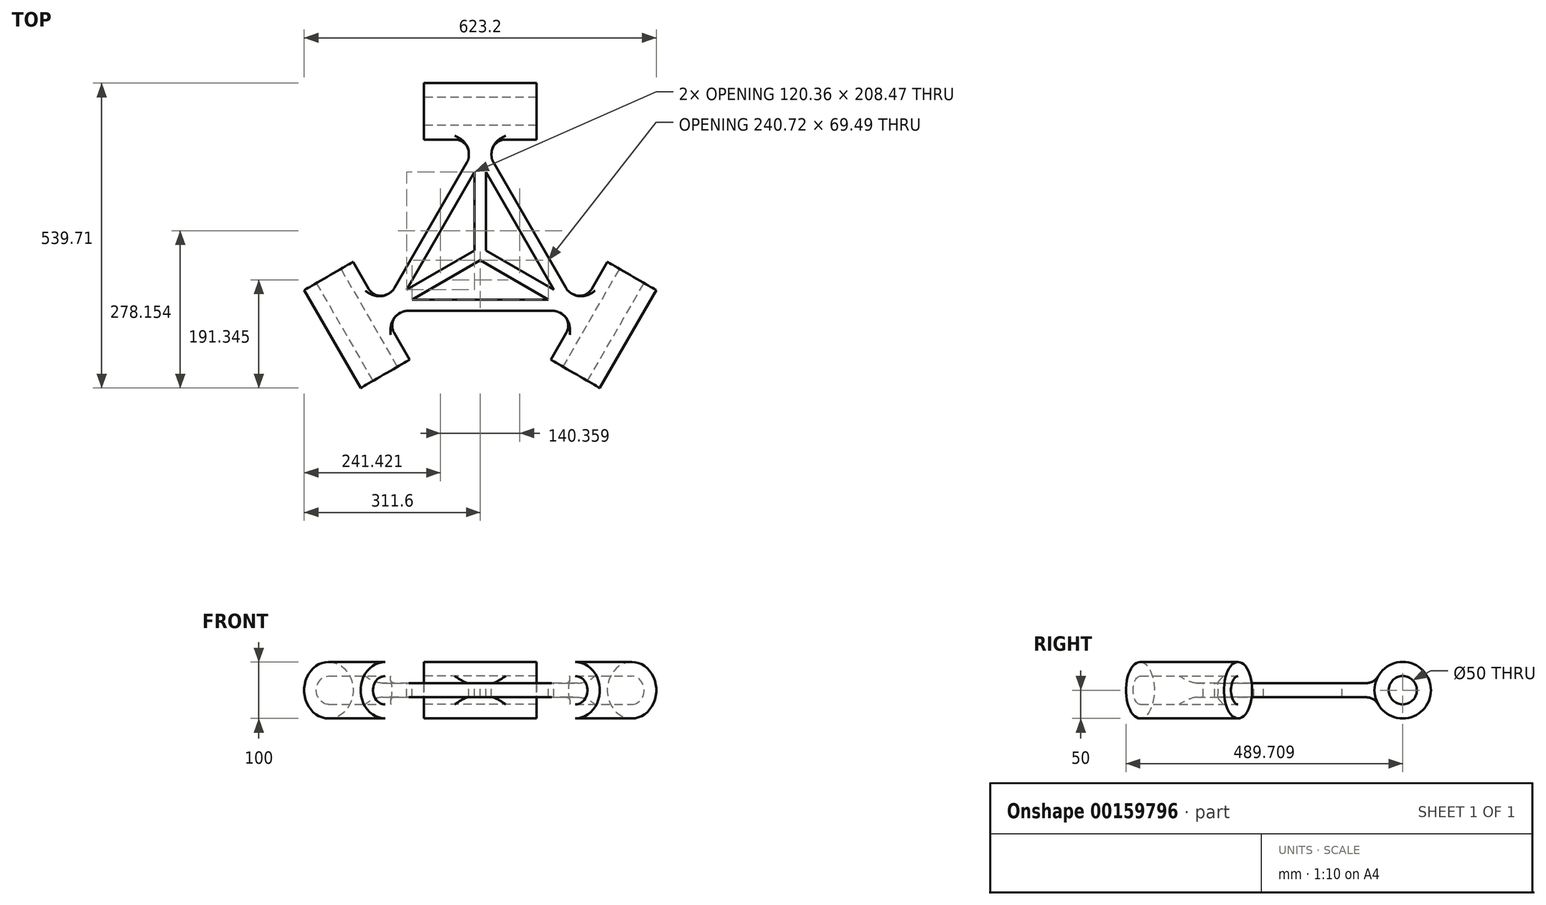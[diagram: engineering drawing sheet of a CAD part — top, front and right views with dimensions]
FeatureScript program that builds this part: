
annotation { "Feature Type Name" : "Feature", "Feature Type Description" : "" }
export const myFeature = defineFeature(function(context is Context, id is Id, definition is map)
    precondition{}
    {
        {
            var Q0;
            Q0=qCreatedBy(makeId("Top.planeOp"),FACE);
            var sketch = newSketch(context, id + "F0", { "sketchPlane" : qUnion([Q0])});
            skLineSegment(sketch, "E0", {"start": v(0, 0) * mm, "end": v(350, 0) * mm});
            skLineSegment(sketch, "E1", {"start": v(0, 0) * mm, "end": v(175, 303.1) * mm});
            skLineSegment(sketch, "E2", {"start": v(175, 303.1) * mm, "end": v(350, 0) * mm});
            skSolve(sketch);
        }
        {
            var Q0;
            Q0=qSketchRegion(id+"F0",true);
            extrude(context, id + "F1", {"entities" : qUnion([Q0]), "depth" : 25 * mm});
        }
        {
            var Q0;
            Q0=qCreatedBy(makeId("Right.planeOp"),FACE);
            var Q1;
            Q1=makeQuery(id+"F1.opExtrude","CAP_VERTEX",VERTEX,{"disambiguationData":[OSD([sQuery(id+"F0.wireOp",EDGE,"E1"),sQuery(id+"F0.wireOp",EDGE,"E2")])],"isStart":false});
            cPlane(context, id + "F2", {"entities" : qUnion([Q0, Q1]), "cplaneType" : CPlaneType.PLANE_POINT, "offset" : 150 * mm, "width" : 150 * mm, "height" : 150 * mm});
        }
        {
            var Q0;
            Q0=qCreatedBy(id+"F2.planeOp",FACE);
            var sketch = newSketch(context, id + "F3", { "sketchPlane" : qUnion([Q0])});
            skLineSegment(sketch, "E3.0", {"start": v(303.1, 25) * mm, "end": v(303.1, 0) * mm});
            skLineSegment(sketch, "E4", {"start": v(303.1, 12.5) * mm, "end": v(353.1, 12.5) * mm});
            skCircle(sketch, "E5", {"center": v(353.1, 12.5) * mm, "radius": 50 * mm});
            skCircle(sketch, "E6", {"center": v(353.1, 12.5) * mm, "radius": 25 * mm});
            skSolve(sketch);
        }
        {
            var Q0;
            Q0=qSketchRegion(id+"F3",true);
            extrude(context, id + "F4", {"entities" : qUnion([Q0]), "endBound" : BoundingType.SYMMETRIC, "depth" : 200 * mm});
        }
        {
            var Q0;
            Q0=makeQuery(id+"F1.opExtrude","CAP_FACE",FACE,{"disambiguationData":[OSD([sQuery(id+"F0.wireOp",EDGE,"E0"),sQuery(id+"F0.wireOp",EDGE,"E1"),sQuery(id+"F0.wireOp",EDGE,"E2")])],"isStart":false});
            var sketch = newSketch(context, id + "F5", { "sketchPlane" : qUnion([Q0])});
            skLineSegment(sketch, "E7", {"start": v(350, 0) * mm, "end": v(87.5, 151.55) * mm});
            skLineSegment(sketch, "E8", {"start": v(0, 0) * mm, "end": v(262.5, 151.55) * mm});
            skSolve(sketch);
        }
        {
            var Q0;
            Q0=qSketchRegion(id+"F5",true);
            var Q1;
            {var subQ1=makeQuery(id+"F1.opExtrude","CAP_EDGE",EDGE,{"disambiguationData":[OSD([sQuery(id+"F0.wireOp",EDGE,"E2")])],"isStart":false});var subQ3=sQuery(id+"F5.wireOp",EDGE,"E8");var subQ5=makeQuery(id+"F5.imprint","INTERSECT",VERTEX,{"derivedFrom":[subQ1,subQ3]});Q1=makeQuery(id+"F5.imprint","IMPRINT",FACE,{"disambiguationData":[TD([[makeQuery(id+"F5.imprint","IMPRINT",EDGE,{"disambiguationData":[TD([[subQ5,1.0]])],"derivedFrom":subQ3}),-1.0]])]});}
            var Q2;
            {var subQ0=sQuery(id+"F5.wireOp",EDGE,"E7");var subQ1=makeQuery(id+"F1.opExtrude","CAP_EDGE",EDGE,{"disambiguationData":[OSD([sQuery(id+"F0.wireOp",EDGE,"E1")])],"isStart":false});var subQ2=makeQuery(id+"F5.imprint","INTERSECT",VERTEX,{"derivedFrom":[subQ1,subQ0]});Q2=makeQuery(id+"F5.imprint","IMPRINT",FACE,{"disambiguationData":[TD([[makeQuery(id+"F5.imprint","IMPRINT",EDGE,{"disambiguationData":[TD([[subQ2,1.0]])],"derivedFrom":subQ0}),1.0]])]});}
            var Q3;
            {var subQ1=makeQuery(id+"F1.opExtrude","CAP_EDGE",EDGE,{"disambiguationData":[OSD([sQuery(id+"F0.wireOp",EDGE,"E0")])],"isStart":false});Q3=makeQuery(id+"F5.imprint","IMPRINT",FACE,{"disambiguationData":[TD([[makeQuery(id+"F5.imprint","IMPRINT",EDGE,{"derivedFrom":subQ1}),1.0]])]});}
            extrude(context, id + "F6", {"entities" : qUnion([Q0, Q1, Q2, Q3]), "operationType" : NewBodyOperationType.REMOVE, "endBound" : BoundingType.THROUGH_ALL, "oppositeDirection" : true, "depth" : 25 * mm});
        }
        {
            var Q0;
            Q0=qCreatedBy(makeId("Front.planeOp"),FACE);
            var Q1;
            Q1=makeQuery(id+"F1.opExtrude","CAP_VERTEX",VERTEX,{"disambiguationData":[OSD([sQuery(id+"F0.wireOp",EDGE,"E1"),sQuery(id+"F0.wireOp",EDGE,"E2")])],"isStart":false});
            cPlane(context, id + "F7", {"entities" : qUnion([Q0, Q1]), "cplaneType" : CPlaneType.PLANE_POINT, "offset" : 150 * mm, "width" : 150 * mm, "height" : 150 * mm});
        }
        {
            var Q0;
            Q0=qCreatedBy(id+"F7.planeOp",FACE);
            var sketch = newSketch(context, id + "F8", { "sketchPlane" : qUnion([Q0])});
            skLineSegment(sketch, "E9.0", {"start": v(175, 0) * mm, "end": v(175, 25) * mm});
            skLineSegment(sketch, "E10", {"start": v(175, 25) * mm, "end": v(155, 25) * mm});
            skLineSegment(sketch, "E11.bottom", {"start": v(155, 25) * mm, "end": v(195, 25) * mm});
            skLineSegment(sketch, "E11.top", {"start": v(155, 0) * mm, "end": v(195, 0) * mm});
            skLineSegment(sketch, "E11.left", {"start": v(155, 25) * mm, "end": v(155, 0) * mm});
            skLineSegment(sketch, "E11.right", {"start": v(195, 25) * mm, "end": v(195, 0) * mm});
            skSolve(sketch);
        }
        {
            var Q0;
            Q0=qSketchRegion(id+"F8",true);
            var Q1;
            Q1=makeQuery(id+"F1.opExtrude","SWEPT_BODY",BODY,{"disambiguationData":[OSD([sQuery(id+"F0.wireOp",EDGE,"E0"),sQuery(id+"F0.wireOp",EDGE,"E1"),sQuery(id+"F0.wireOp",EDGE,"E2")])]});
            extrude(context, id + "F9", {"entities" : qUnion([Q0]), "endBoundEntityBody" : qUnion([Q1]), "depth" : 50 * mm});
        }
        {
            var Q0;
            Q0=makeQuery(id+"F9.opExtrude","SWEPT_BODY",BODY,{"disambiguationData":[OSD([sQuery(id+"F8.wireOp",EDGE,"E11.bottom"),sQuery(id+"F8.wireOp",EDGE,"E11.top"),sQuery(id+"F8.wireOp",EDGE,"E11.left"),sQuery(id+"F8.wireOp",EDGE,"E11.right")])]});
            var Q1;
            Q1=makeQuery(id+"F1.opExtrude","SWEPT_BODY",BODY,{"disambiguationData":[OSD([sQuery(id+"F0.wireOp",EDGE,"E0"),sQuery(id+"F0.wireOp",EDGE,"E1"),sQuery(id+"F0.wireOp",EDGE,"E2")])]});
            booleanBodies(context, id + "F10", {"operationType" : BooleanOperationType.UNION, "tools" : qUnion([Q0, Q1])});
        }
        {
            var Q0;
            Q0=makeQuery(id+"F9.opExtrude","CAP_FACE",FACE,{"disambiguationData":[OSD([sQuery(id+"F8.wireOp",EDGE,"E11.bottom"),sQuery(id+"F8.wireOp",EDGE,"E11.top"),sQuery(id+"F8.wireOp",EDGE,"E11.left"),sQuery(id+"F8.wireOp",EDGE,"E11.right")])],"isStart":true});
            extrude(context, id + "F11", {"entities" : qUnion([Q0]), "depth" : 15 * mm});
        }
        {
            var Q0;
            Q0=makeQuery(id+"F11.opExtrude","SWEPT_BODY",BODY,{"disambiguationData":[OSD([sQuery(id+"F8.wireOp",EDGE,"E11.bottom"),sQuery(id+"F8.wireOp",EDGE,"E11.top"),sQuery(id+"F8.wireOp",EDGE,"E11.left"),sQuery(id+"F8.wireOp",EDGE,"E11.right")])]});
            var Q1;
            Q1=makeQuery(id+"F9.opExtrude","SWEPT_BODY",BODY,{"disambiguationData":[OSD([sQuery(id+"F8.wireOp",EDGE,"E11.bottom"),sQuery(id+"F8.wireOp",EDGE,"E11.top"),sQuery(id+"F8.wireOp",EDGE,"E11.left"),sQuery(id+"F8.wireOp",EDGE,"E11.right")])]});
            booleanBodies(context, id + "F12", {"operationType" : BooleanOperationType.UNION, "tools" : qUnion([Q0, Q1])});
        }
        {
            var Q0;
            Q0=makeQuery(id+"F4.opExtrude","SWEPT_BODY",BODY,{"disambiguationData":[OSD([sQuery(id+"F3.wireOp",EDGE,"E5"),sQuery(id+"F3.wireOp",EDGE,"E6")])]});
            var Q1;
            Q1=makeQuery(id+"F11.opExtrude","SWEPT_BODY",BODY,{"disambiguationData":[OSD([sQuery(id+"F8.wireOp",EDGE,"E11.bottom"),sQuery(id+"F8.wireOp",EDGE,"E11.top"),sQuery(id+"F8.wireOp",EDGE,"E11.left"),sQuery(id+"F8.wireOp",EDGE,"E11.right")])]});
            booleanBodies(context, id + "F13", {"operationType" : BooleanOperationType.UNION, "tools" : qUnion([Q0, Q1])});
        }
        {
            var Q0;
            {var subQ0=sQuery(id+"F8.wireOp",EDGE,"E11.bottom");Q0=makeQuery(id+"F13.opBoolean","INTERSECT",EDGE,{"derivedFrom":[makeQuery(id+"F4.opExtrude","SWEPT_FACE",FACE,{"disambiguationData":[OSD([sQuery(id+"F3.wireOp",EDGE,"E5")])]}),makeQuery(id+"F12.opBoolean","MERGE",FACE,{"derivedFrom":[makeQuery(id+"F10.opBoolean","MERGE",FACE,{"derivedFrom":[makeQuery(id+"F1.opExtrude","CAP_FACE",FACE,{"disambiguationData":[OSD([sQuery(id+"F0.wireOp",EDGE,"E0"),sQuery(id+"F0.wireOp",EDGE,"E1"),sQuery(id+"F0.wireOp",EDGE,"E2")])],"isStart":false}),makeQuery(id+"F9.opExtrude","SWEPT_FACE",FACE,{"disambiguationData":[OSD([subQ0])]})]}),makeQuery(id+"F11.opExtrude","SWEPT_FACE",FACE,{"disambiguationData":[OSD([subQ0])]})]})]});}
            var Q1;
            {var subQ0=sQuery(id+"F8.wireOp",EDGE,"E11.top");Q1=makeQuery(id+"F13.opBoolean","INTERSECT",EDGE,{"derivedFrom":[makeQuery(id+"F4.opExtrude","SWEPT_FACE",FACE,{"disambiguationData":[OSD([sQuery(id+"F3.wireOp",EDGE,"E5")])]}),makeQuery(id+"F12.opBoolean","MERGE",FACE,{"derivedFrom":[makeQuery(id+"F10.opBoolean","MERGE",FACE,{"derivedFrom":[makeQuery(id+"F1.opExtrude","CAP_FACE",FACE,{"disambiguationData":[OSD([sQuery(id+"F0.wireOp",EDGE,"E0"),sQuery(id+"F0.wireOp",EDGE,"E1"),sQuery(id+"F0.wireOp",EDGE,"E2")])],"isStart":true}),makeQuery(id+"F9.opExtrude","SWEPT_FACE",FACE,{"disambiguationData":[OSD([subQ0])]})]}),makeQuery(id+"F11.opExtrude","SWEPT_FACE",FACE,{"disambiguationData":[OSD([subQ0])]})]})]});}
            fillet(context, id + "F14", {"entities" : qUnion([Q0, Q1]), "radius" : 25 * mm, "tangentPropagation" : true, "allowEdgeOverflow" : false});
        }
        {
            var Q0;
            {var subQ0=sQuery(id+"F8.wireOp",EDGE,"E11.right");Q0=makeQuery(id+"F13.opBoolean","INTERSECT",EDGE,{"derivedFrom":[makeQuery(id+"F4.opExtrude","SWEPT_FACE",FACE,{"disambiguationData":[OSD([sQuery(id+"F3.wireOp",EDGE,"E5")])]}),makeQuery(id+"F12.opBoolean","MERGE",FACE,{"derivedFrom":[makeQuery(id+"F9.opExtrude","SWEPT_FACE",FACE,{"disambiguationData":[OSD([subQ0])]}),makeQuery(id+"F11.opExtrude","SWEPT_FACE",FACE,{"disambiguationData":[OSD([subQ0])]})]})]});}
            var Q1;
            {var subQ0=sQuery(id+"F8.wireOp",EDGE,"E11.left");Q1=makeQuery(id+"F13.opBoolean","INTERSECT",EDGE,{"derivedFrom":[makeQuery(id+"F4.opExtrude","SWEPT_FACE",FACE,{"disambiguationData":[OSD([sQuery(id+"F3.wireOp",EDGE,"E5")])]}),makeQuery(id+"F12.opBoolean","MERGE",FACE,{"derivedFrom":[makeQuery(id+"F9.opExtrude","SWEPT_FACE",FACE,{"disambiguationData":[OSD([subQ0])]}),makeQuery(id+"F11.opExtrude","SWEPT_FACE",FACE,{"disambiguationData":[OSD([subQ0])]})]})]});}
            fillet(context, id + "F15", {"entities" : qUnion([Q0, Q1]), "radius" : 25 * mm, "tangentPropagation" : true, "allowEdgeOverflow" : false});
        }
        {
            var Q0;
            Q0=makeQuery(id+"F10.opBoolean","INTERSECT",EDGE,{"derivedFrom":[makeQuery(id+"F1.opExtrude","SWEPT_FACE",FACE,{"disambiguationData":[OSD([sQuery(id+"F0.wireOp",EDGE,"E1")])]}),makeQuery(id+"F9.opExtrude","SWEPT_FACE",FACE,{"disambiguationData":[OSD([sQuery(id+"F8.wireOp",EDGE,"E11.left")])]})]});
            var Q1;
            Q1=makeQuery(id+"F10.opBoolean","INTERSECT",EDGE,{"derivedFrom":[makeQuery(id+"F1.opExtrude","SWEPT_FACE",FACE,{"disambiguationData":[OSD([sQuery(id+"F0.wireOp",EDGE,"E2")])]}),makeQuery(id+"F9.opExtrude","SWEPT_FACE",FACE,{"disambiguationData":[OSD([sQuery(id+"F8.wireOp",EDGE,"E11.right")])]})]});
            fillet(context, id + "F16", {"entities" : qUnion([Q0, Q1]), "radius" : 25 * mm, "tangentPropagation" : true, "allowEdgeOverflow" : false});
        }
        {
            var Q0;
            Q0=qCreatedBy(makeId("Right.planeOp"),FACE);
            var Q1;
            Q1=makeQuery(id+"F6.boolean.opBoolean","COPY",VERTEX,{"derivedFrom":makeQuery(id+"F6.opExtrude","CAP_VERTEX",VERTEX,{"disambiguationData":[OSD([sQuery(id+"F5.wireOp",EDGE,"E7"),sQuery(id+"F5.wireOp",EDGE,"E8")])],"isStart":true})});
            cPlane(context, id + "F17", {"entities" : qUnion([Q0, Q1]), "cplaneType" : CPlaneType.PLANE_POINT, "offset" : 150 * mm, "width" : 150 * mm, "height" : 150 * mm});
        }
        {
            var Q0;
            Q0=qCreatedBy(id+"F17.planeOp",FACE);
            var sketch = newSketch(context, id + "F18", { "sketchPlane" : qUnion([Q0])});
            skLineSegment(sketch, "E12.0", {"start": v(101.04, 0) * mm, "end": v(101.04, 25) * mm});
            skLineSegment(sketch, "E13", {"start": v(101.04, 25) * mm, "end": v(101.04, 40.8) * mm});
            skSolve(sketch);
        }
        {
            var Q0;
            Q0=makeQuery(id+"F4.opExtrude","SWEPT_BODY",BODY,{"disambiguationData":[OSD([sQuery(id+"F3.wireOp",EDGE,"E5"),sQuery(id+"F3.wireOp",EDGE,"E6")])]});
            var Q1;
            Q1=sQuery(id+"F18.wireOp",EDGE,"E13");
            circularPattern(context, id + "F19", {"entities" : qUnion([Q0]), "axis" : qUnion([Q1]), "angle" : 120 * degree, "instanceCount" : 3});
        }
        {
            var Q0;
            Q0=makeQuery(id+"F4.opExtrude","SWEPT_BODY",BODY,{"disambiguationData":[OSD([sQuery(id+"F3.wireOp",EDGE,"E5"),sQuery(id+"F3.wireOp",EDGE,"E6")])]});
            var Q1;
            Q1=makeQuery(id+"F19.opPattern","COPY",BODY,{"derivedFrom":makeQuery(id+"F4.opExtrude","SWEPT_BODY",BODY,{"disambiguationData":[OSD([sQuery(id+"F3.wireOp",EDGE,"E5"),sQuery(id+"F3.wireOp",EDGE,"E6")])]}),"instanceName":"2"});
            var Q2;
            Q2=makeQuery(id+"F19.opPattern","COPY",BODY,{"derivedFrom":makeQuery(id+"F4.opExtrude","SWEPT_BODY",BODY,{"disambiguationData":[OSD([sQuery(id+"F3.wireOp",EDGE,"E5"),sQuery(id+"F3.wireOp",EDGE,"E6")])]}),"instanceName":"1"});
            booleanBodies(context, id + "F20", {"operationType" : BooleanOperationType.UNION, "tools" : qUnion([Q0, Q1, Q2])});
        }
        {
            var Q0;
            {var subQ0=sQuery(id+"F8.wireOp",EDGE,"E11.bottom");var subQ1=makeQuery(id+"F12.opBoolean","MERGE",FACE,{"derivedFrom":[makeQuery(id+"F10.opBoolean","MERGE",FACE,{"derivedFrom":[makeQuery(id+"F1.opExtrude","CAP_FACE",FACE,{"disambiguationData":[OSD([sQuery(id+"F0.wireOp",EDGE,"E0"),sQuery(id+"F0.wireOp",EDGE,"E1"),sQuery(id+"F0.wireOp",EDGE,"E2")])],"isStart":false}),makeQuery(id+"F9.opExtrude","SWEPT_FACE",FACE,{"disambiguationData":[OSD([subQ0])]})]}),makeQuery(id+"F11.opExtrude","SWEPT_FACE",FACE,{"disambiguationData":[OSD([subQ0])]})]});Q0=makeQuery(id+"F20.opBoolean","MERGE",FACE,{"derivedFrom":[subQ1,makeQuery(id+"F19.opPattern","COPY",FACE,{"derivedFrom":subQ1,"instanceName":"1"}),makeQuery(id+"F19.opPattern","COPY",FACE,{"derivedFrom":subQ1,"instanceName":"2"})]});}
            var sketch = newSketch(context, id + "F21", { "sketchPlane" : qUnion([Q0])});
            skLineSegment(sketch, "E14.0.0", {"start": v(151.65, 262.67) * mm, "end": v(23.35, 40.44) * mm});
            skArc(sketch, "E14.0.1", {"start": v(23.35, 40.44) * mm, "mid": v(19.38, 35.26) * mm, "end": v(14.2, 31.3) * mm});
            skLineSegment(sketch, "E14.0.2", {"start": v(14.2, 31.3) * mm, "end": v(10.74, 29.3) * mm});
            skFitSpline(sketch, "E14.0.3", {"points": [v(10.74, 29.3) * mm, v(9.4, 28.52) * mm, v(6.62, 27.24) * mm, v(3.66, 26.46) * mm, v(2.14, 26.2) * mm]});
            skLineSegment(sketch, "E14.0.4", {"start": v(2.14, 26.2) * mm, "end": v(23.76, -11.25) * mm});
            skFitSpline(sketch, "E14.0.5", {"points": [v(23.76, -11.25) * mm, v(24.75, -10.06) * mm, v(26.9, -7.88) * mm, v(29.4, -6.12) * mm, v(30.74, -5.35) * mm]});
            skLineSegment(sketch, "E14.0.6", {"start": v(30.74, -5.35) * mm, "end": v(34.2, -3.35) * mm});
            skArc(sketch, "E14.0.7", {"start": v(34.2, -3.35) * mm, "mid": v(40.23, -0.85) * mm, "end": v(46.7, 0) * mm});
            skLineSegment(sketch, "E14.0.8", {"start": v(46.7, 0) * mm, "end": v(303.3, 0) * mm});
            skArc(sketch, "E14.0.9", {"start": v(303.3, 0) * mm, "mid": v(309.77, -0.85) * mm, "end": v(315.8, -3.35) * mm});
            skLineSegment(sketch, "E14.0.10", {"start": v(315.8, -3.35) * mm, "end": v(319.26, -5.35) * mm});
            skFitSpline(sketch, "E14.0.11", {"points": [v(319.26, -5.35) * mm, v(320.6, -6.12) * mm, v(323.1, -7.88) * mm, v(325.25, -10.06) * mm, v(326.24, -11.25) * mm]});
            skLineSegment(sketch, "E14.0.12", {"start": v(326.24, -11.25) * mm, "end": v(347.86, 26.2) * mm});
            skFitSpline(sketch, "E14.0.13", {"points": [v(347.86, 26.2) * mm, v(346.34, 26.46) * mm, v(343.38, 27.24) * mm, v(340.6, 28.52) * mm, v(339.26, 29.3) * mm]});
            skLineSegment(sketch, "E14.0.14", {"start": v(339.26, 29.3) * mm, "end": v(335.8, 31.3) * mm});
            skArc(sketch, "E14.0.15", {"start": v(335.8, 31.3) * mm, "mid": v(330.62, 35.26) * mm, "end": v(326.65, 40.44) * mm});
            skLineSegment(sketch, "E14.0.16", {"start": v(326.65, 40.44) * mm, "end": v(198.35, 262.67) * mm});
            skArc(sketch, "E14.0.17", {"start": v(198.35, 262.67) * mm, "mid": v(195.85, 268.7) * mm, "end": v(195, 275.17) * mm});
            skLineSegment(sketch, "E14.0.18", {"start": v(195, 275.17) * mm, "end": v(195, 279.16) * mm});
            skFitSpline(sketch, "E14.0.19", {"points": [v(195, 279.16) * mm, v(195, 280.7) * mm, v(195.28, 283.75) * mm, v(196.08, 286.7) * mm, v(196.62, 288.16) * mm]});
            skLineSegment(sketch, "E14.0.20", {"start": v(196.62, 288.16) * mm, "end": v(153.38, 288.16) * mm});
            skFitSpline(sketch, "E14.0.21", {"points": [v(153.38, 288.16) * mm, v(153.92, 286.7) * mm, v(154.72, 283.75) * mm, v(155, 280.7) * mm, v(155, 279.16) * mm]});
            skLineSegment(sketch, "E14.0.22", {"start": v(155, 279.16) * mm, "end": v(155, 275.17) * mm});
            skArc(sketch, "E14.0.23", {"start": v(155, 275.17) * mm, "mid": v(154.15, 268.7) * mm, "end": v(151.65, 262.67) * mm});
            skLineSegment(sketch, "E15.0", {"start": v(168.97, 252.67) * mm, "end": v(40.67, 30.44) * mm});
            skLineSegment(sketch, "E16.0", {"start": v(309.33, 30.44) * mm, "end": v(181.03, 252.67) * mm});
            skLineSegment(sketch, "E17.0", {"start": v(46.7, 20) * mm, "end": v(303.3, 20) * mm});
            skLineSegment(sketch, "E18", {"start": v(40.67, 30.44) * mm, "end": v(46.7, 20) * mm});
            skLineSegment(sketch, "E19", {"start": v(309.33, 30.44) * mm, "end": v(303.3, 20) * mm});
            skLineSegment(sketch, "E20", {"start": v(168.97, 252.67) * mm, "end": v(181.03, 252.67) * mm});
            skLineSegment(sketch, "E21", {"start": v(175, 252.67) * mm, "end": v(175, 101.04) * mm});
            skLineSegment(sketch, "E22", {"start": v(43.68, 25.22) * mm, "end": v(175, 101.04) * mm});
            skLineSegment(sketch, "E23", {"start": v(306.32, 25.22) * mm, "end": v(175, 101.04) * mm});
            skPoint(sketch, "E24.orphan", {"position": v(175, 20) * mm});
            skPoint(sketch, "E25.orphan", {"position": v(245.18, 141.55) * mm});
            skLineSegment(sketch, "E26.0", {"start": v(301.32, 16.56) * mm, "end": v(175, 89.49) * mm});
            skLineSegment(sketch, "E26.1", {"start": v(48.68, 16.56) * mm, "end": v(175, 89.49) * mm});
            skLineSegment(sketch, "E27.0", {"start": v(170, 252.67) * mm, "end": v(170, 103.92) * mm});
            skLineSegment(sketch, "E27.1", {"start": v(41.18, 29.55) * mm, "end": v(170, 103.92) * mm});
            skLineSegment(sketch, "E28.0", {"start": v(38.68, 33.88) * mm, "end": v(167.5, 108.25) * mm});
            skLineSegment(sketch, "E29.0", {"start": v(165, 252.67) * mm, "end": v(165, 103.92) * mm});
            skLineSegment(sketch, "E30.0", {"start": v(185, 252.67) * mm, "end": v(185, 106.8) * mm});
            skLineSegment(sketch, "E30.1", {"start": v(311.32, 33.88) * mm, "end": v(185, 106.8) * mm});
            skSolve(sketch);
        }
        {
            var Q0;
            {var subQ0=sQuery(id+"F21.wireOp",EDGE,"E29.0");var subQ1=sQuery(id+"F21.wireOp",EDGE,"E15.0");var subQ2=makeQuery(id+"F21.imprint","INTERSECT",VERTEX,{"derivedFrom":[subQ1,subQ0]});Q0=makeQuery(id+"F21.imprint","IMPRINT",FACE,{"disambiguationData":[TD([[makeQuery(id+"F21.imprint","IMPRINT",EDGE,{"disambiguationData":[TD([[subQ2,-1.0]])],"derivedFrom":subQ1}),1.0]])]});}
            var Q1;
            {var subQ0=sQuery(id+"F21.wireOp",EDGE,"E30.1");var subQ1=sQuery(id+"F21.wireOp",EDGE,"E16.0");var subQ2=makeQuery(id+"F21.imprint","INTERSECT",VERTEX,{"derivedFrom":[subQ1,subQ0]});Q1=makeQuery(id+"F21.imprint","IMPRINT",FACE,{"disambiguationData":[TD([[makeQuery(id+"F21.imprint","IMPRINT",EDGE,{"disambiguationData":[TD([[subQ2,-1.0]])],"derivedFrom":subQ1}),1.0]])]});}
            var Q2;
            {var subQ0=sQuery(id+"F21.wireOp",EDGE,"E26.1");var subQ1=sQuery(id+"F21.wireOp",EDGE,"E17.0");var subQ2=makeQuery(id+"F21.imprint","INTERSECT",VERTEX,{"derivedFrom":[subQ1,subQ0]});Q2=makeQuery(id+"F21.imprint","IMPRINT",FACE,{"disambiguationData":[TD([[makeQuery(id+"F21.imprint","IMPRINT",EDGE,{"disambiguationData":[TD([[subQ2,-1.0]])],"derivedFrom":subQ1}),1.0]])]});}
            extrude(context, id + "F22", {"entities" : qUnion([Q0, Q1, Q2]), "operationType" : NewBodyOperationType.REMOVE, "endBound" : BoundingType.THROUGH_ALL, "oppositeDirection" : true, "depth" : 25 * mm});
        }
    });
